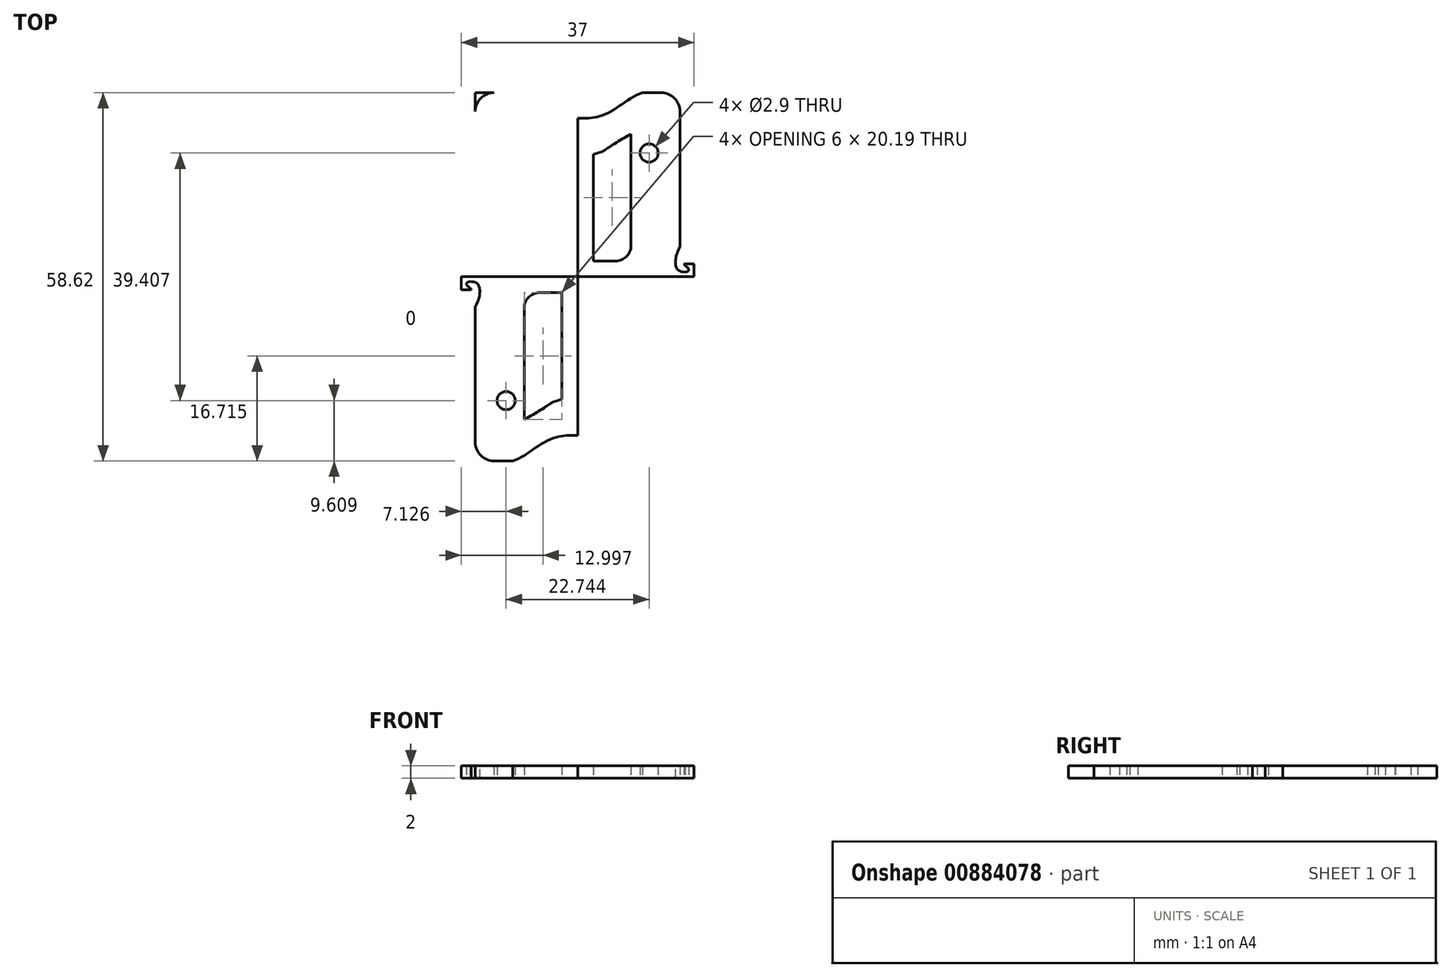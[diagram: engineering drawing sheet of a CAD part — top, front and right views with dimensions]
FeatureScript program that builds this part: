
annotation { "Feature Type Name" : "Feature", "Feature Type Description" : "" }
export const myFeature = defineFeature(function(context is Context, id is Id, definition is map)
    precondition{}
    {
        {
            var Q0;
            Q0=qCreatedBy(makeId("Top.planeOp"),FACE);
            var sketch = newSketch(context, id + "F0", { "sketchPlane" : qUnion([Q0])});
            skLineSegment(sketch, "E0.bottom", {"start": v(10.05, 48.23) * mm, "end": v(16.04, 48.23) * mm});
            skLineSegment(sketch, "E0.top", {"start": v(13.05, -10.39) * mm, "end": v(16.04, -10.39) * mm});
            skLineSegment(sketch, "E0.left", {"start": v(10.05, 48.23) * mm, "end": v(10.05, 23.75) * mm});
            skFitSpline(sketch, "E1", {"points": [v(42.63, 48.23) * mm, v(36.63, 48.23) * mm, v(30.94, 44.88) * mm, v(26.34, 44.13) * mm], "startDerivative": vector(-19.72, 0) * mm, "endDerivative": vector(-14.92, -0.07) * mm});
            skFitSpline(sketch, "E2.MirrorCS", {"points": [v(10.05, 48.23) * mm, v(16.04, 48.23) * mm, v(21.74, 44.88) * mm, v(26.34, 44.13) * mm], "startDerivative": vector(19.72, 0) * mm, "endDerivative": vector(14.92, -0.07) * mm});
            skFitSpline(sketch, "E3.MirrorCS", {"points": [v(42.63, -10.39) * mm, v(36.63, -10.39) * mm, v(30.94, -7.03) * mm, v(26.34, -6.29) * mm], "startDerivative": vector(-19.72, 0) * mm, "endDerivative": vector(-14.92, 0.07) * mm});
            skFitSpline(sketch, "E4.MirrorCS", {"points": [v(10.05, -10.39) * mm, v(16.04, -10.39) * mm, v(21.74, -7.03) * mm, v(26.34, -6.29) * mm], "startDerivative": vector(19.72, 0) * mm, "endDerivative": vector(14.92, 0.07) * mm});
            skLineSegment(sketch, "E5.trimOffspring", {"start": v(36.63, 48.23) * mm, "end": v(42.63, 48.23) * mm});
            skLineSegment(sketch, "E6.trimOffspring", {"start": v(36.63, -10.39) * mm, "end": v(42.63, -10.39) * mm});
            skArc(sketch, "E7.filletArc", {"start": v(10.05, -7.39) * mm, "mid": v(10.92, -9.5) * mm, "end": v(13.05, -10.39) * mm});
            skArc(sketch, "E8.MirrorCS", {"start": v(42.63, -7.39) * mm, "mid": v(41.75, -9.5) * mm, "end": v(39.63, -10.39) * mm});
            skArc(sketch, "E9.MirrorCS", {"start": v(42.63, 45.23) * mm, "mid": v(41.75, 47.35) * mm, "end": v(39.63, 48.23) * mm});
            skArc(sketch, "E10.MirrorCS", {"start": v(10.05, 45.23) * mm, "mid": v(10.92, 47.35) * mm, "end": v(13.05, 48.23) * mm});
            skCircle(sketch, "E11", {"center": v(14.97, 38.63) * mm, "radius": 1.45 * mm});
            skFitSpline(sketch, "E12", {"points": [v(10.05, 23.75) * mm, v(10.74, 20.73) * mm, v(9.24, 19.67) * mm], "startDerivative": vector(3.54, -6.71) * mm, "endDerivative": vector(-7.62, -0.35) * mm});
            skLineSegment(sketch, "E13", {"start": v(8.28, 20.96) * mm, "end": v(7.84, 20.96) * mm});
            skLineSegment(sketch, "E14", {"start": v(7.84, 20.96) * mm, "end": v(7.84, 18.92) * mm});
            skLineSegment(sketch, "E15.MirrorCS", {"start": v(7.84, 16.88) * mm, "end": v(7.84, 18.92) * mm});
            skLineSegment(sketch, "E16.MirrorCS", {"start": v(8.28, 16.88) * mm, "end": v(7.84, 16.88) * mm});
            skFitSpline(sketch, "E17.MirrorCS", {"points": [v(10.05, 14.1) * mm, v(10.74, 17.11) * mm, v(9.24, 18.18) * mm], "startDerivative": vector(3.54, 6.71) * mm, "endDerivative": vector(-7.62, 0.35) * mm});
            skLineSegment(sketch, "E18", {"start": v(8.28, 20.96) * mm, "end": v(9.38, 20.96) * mm});
            skFitSpline(sketch, "E19", {"points": [v(9.38, 20.96) * mm, v(8.76, 20.32) * mm, v(9.24, 19.67) * mm], "startDerivative": vector(0.5, -1.03) * mm, "endDerivative": vector(3.51, -0.24) * mm});
            skFitSpline(sketch, "E20.MirrorCS", {"points": [v(9.38, 16.88) * mm, v(8.76, 17.53) * mm, v(9.24, 18.18) * mm], "startDerivative": vector(0.5, 1.03) * mm, "endDerivative": vector(3.51, 0.24) * mm});
            skLineSegment(sketch, "E21.MirrorCS", {"start": v(8.28, 16.88) * mm, "end": v(9.38, 16.88) * mm});
            skPoint(sketch, "E22.orphan", {"position": v(8.28, 16.88) * mm});
            skLineSegment(sketch, "E23.trimOffspring", {"start": v(10.05, 14.1) * mm, "end": v(10.05, -7.39) * mm});
            skFitSpline(sketch, "E24.MirrorCS", {"points": [v(42.63, 23.75) * mm, v(41.94, 20.73) * mm, v(43.44, 19.67) * mm], "startDerivative": vector(-3.54, -6.71) * mm, "endDerivative": vector(7.62, -0.35) * mm});
            skFitSpline(sketch, "E25.MirrorCS", {"points": [v(42.63, 14.1) * mm, v(41.94, 17.11) * mm, v(43.44, 18.18) * mm], "startDerivative": vector(-3.54, 6.71) * mm, "endDerivative": vector(7.62, 0.35) * mm});
            skFitSpline(sketch, "E26.MirrorCS", {"points": [v(43.3, 16.88) * mm, v(43.91, 17.53) * mm, v(43.44, 18.18) * mm], "startDerivative": vector(-0.5, 1.03) * mm, "endDerivative": vector(-3.51, 0.24) * mm});
            skFitSpline(sketch, "E27.MirrorCS", {"points": [v(43.3, 20.96) * mm, v(43.91, 20.32) * mm, v(43.44, 19.67) * mm], "startDerivative": vector(-0.5, -1.03) * mm, "endDerivative": vector(-3.51, -0.24) * mm});
            skLineSegment(sketch, "E28.MirrorCS", {"start": v(44.4, 20.96) * mm, "end": v(43.3, 20.96) * mm});
            skLineSegment(sketch, "E29.MirrorCS", {"start": v(44.4, 20.96) * mm, "end": v(44.84, 20.96) * mm});
            skLineSegment(sketch, "E30.MirrorCS", {"start": v(44.4, 16.88) * mm, "end": v(43.3, 16.88) * mm});
            skLineSegment(sketch, "E31.MirrorCS", {"start": v(44.4, 16.88) * mm, "end": v(44.84, 16.88) * mm});
            skLineSegment(sketch, "E32.MirrorCS", {"start": v(44.84, 16.88) * mm, "end": v(44.84, 18.92) * mm});
            skLineSegment(sketch, "E33.MirrorCS", {"start": v(44.84, 20.96) * mm, "end": v(44.84, 18.92) * mm});
            skLineSegment(sketch, "E34", {"start": v(42.63, 45.23) * mm, "end": v(42.63, 23.75) * mm});
            skLineSegment(sketch, "E35", {"start": v(42.63, 14.1) * mm, "end": v(42.63, -7.39) * mm});
            skCircle(sketch, "E36.MirrorC", {"center": v(37.7, 38.63) * mm, "radius": 1.45 * mm});
            skLineSegment(sketch, "E37", {"start": v(26.34, 44.13) * mm, "end": v(26.34, -6.29) * mm});
            skLineSegment(sketch, "E38", {"start": v(7.84, 18.92) * mm, "end": v(44.84, 18.92) * mm});
            skCircle(sketch, "E39.MirrorC", {"center": v(14.97, -0.78) * mm, "radius": 1.45 * mm});
            skCircle(sketch, "E40.MirrorC", {"center": v(37.7, -0.78) * mm, "radius": 1.45 * mm});
            skLineSegment(sketch, "E41", {"start": v(23.84, 38.43) * mm, "end": v(23.84, 23.16) * mm});
            skLineSegment(sketch, "E42", {"start": v(22.23, 21.42) * mm, "end": v(20.34, 21.42) * mm});
            skLineSegment(sketch, "E43", {"start": v(17.84, 23.92) * mm, "end": v(17.84, 38.92) * mm});
            skPoint(sketch, "E44.visualSharp", {"position": v(23.84, 21.42) * mm});
            skPoint(sketch, "E45.visualSharp", {"position": v(17.84, 21.42) * mm});
            skArc(sketch, "E45.filletArc", {"start": v(17.84, 23.92) * mm, "mid": v(18.57, 22.15) * mm, "end": v(20.34, 21.42) * mm});
            skLineSegment(sketch, "E46", {"start": v(23.84, 23.16) * mm, "end": v(23.84, 21.42) * mm});
            skLineSegment(sketch, "E47", {"start": v(23.84, 21.42) * mm, "end": v(22.23, 21.42) * mm});
            skFitSpline(sketch, "E48.MirrorCS", {"points": [v(23.88, 38.42) * mm, v(21.77, 39.25) * mm, v(17.88, 41.61) * mm], "startDerivative": vector(-9.86, 2.36) * mm, "endDerivative": vector(-7.93, 3.79) * mm});
            skLineSegment(sketch, "E49", {"start": v(17.84, 38.92) * mm, "end": v(17.87, 41.62) * mm});
            skLineSegment(sketch, "E50", {"start": v(17.88, 41.61) * mm, "end": v(17.87, 41.62) * mm});
            skLineSegment(sketch, "E51.MirrorCS", {"start": v(34.8, 41.61) * mm, "end": v(34.8, 41.62) * mm});
            skLineSegment(sketch, "E52.MirrorCS", {"start": v(28.84, 21.42) * mm, "end": v(30.45, 21.42) * mm});
            skLineSegment(sketch, "E53.MirrorCS", {"start": v(28.84, 23.16) * mm, "end": v(28.84, 21.42) * mm});
            skPoint(sketch, "E54.MirrorP", {"position": v(28.84, 21.42) * mm});
            skLineSegment(sketch, "E55.MirrorCS", {"start": v(28.84, 38.43) * mm, "end": v(28.84, 23.16) * mm});
            skPoint(sketch, "E56.MirrorP", {"position": v(34.84, 21.42) * mm});
            skArc(sketch, "E57.MirrorCS", {"start": v(34.84, 23.92) * mm, "mid": v(34.1, 22.15) * mm, "end": v(32.34, 21.42) * mm});
            skLineSegment(sketch, "E58.MirrorCS", {"start": v(30.45, 21.42) * mm, "end": v(32.34, 21.42) * mm});
            skLineSegment(sketch, "E59.MirrorCS", {"start": v(34.84, 23.92) * mm, "end": v(34.84, 38.92) * mm});
            skLineSegment(sketch, "E60.MirrorCS", {"start": v(34.84, 38.92) * mm, "end": v(34.8, 41.62) * mm});
            skFitSpline(sketch, "E61.MirrorCS", {"points": [v(28.8, 38.42) * mm, v(30.9, 39.25) * mm, v(34.8, 41.61) * mm], "startDerivative": vector(9.86, 2.36) * mm, "endDerivative": vector(7.93, 3.79) * mm});
            skLineSegment(sketch, "E62.MirrorCS", {"start": v(34.8, -3.77) * mm, "end": v(34.8, -3.77) * mm});
            skLineSegment(sketch, "E63.MirrorCS", {"start": v(28.84, 16.42) * mm, "end": v(30.45, 16.42) * mm});
            skLineSegment(sketch, "E64.MirrorCS", {"start": v(28.84, 14.68) * mm, "end": v(28.84, 16.42) * mm});
            skPoint(sketch, "E65.MirrorP", {"position": v(28.84, 16.42) * mm});
            skLineSegment(sketch, "E66.MirrorCS", {"start": v(34.84, 13.92) * mm, "end": v(34.84, -1.08) * mm});
            skArc(sketch, "E67.MirrorCS", {"start": v(34.84, 13.92) * mm, "mid": v(34.1, 15.7) * mm, "end": v(32.34, 16.42) * mm});
            skLineSegment(sketch, "E68.MirrorCS", {"start": v(30.45, 16.42) * mm, "end": v(32.34, 16.42) * mm});
            skLineSegment(sketch, "E69.MirrorCS", {"start": v(28.84, -0.59) * mm, "end": v(28.84, 14.68) * mm});
            skFitSpline(sketch, "E70.MirrorCS", {"points": [v(28.8, -0.58) * mm, v(30.9, -1.4) * mm, v(34.8, -3.77) * mm], "startDerivative": vector(9.86, -2.36) * mm, "endDerivative": vector(7.93, -3.79) * mm});
            skLineSegment(sketch, "E71.MirrorCS", {"start": v(34.84, -1.08) * mm, "end": v(34.8, -3.77) * mm});
            skPoint(sketch, "E72.MirrorP", {"position": v(34.84, 16.42) * mm});
            skLineSegment(sketch, "E73.MirrorCS", {"start": v(17.88, -3.77) * mm, "end": v(17.87, -3.77) * mm});
            skLineSegment(sketch, "E74.MirrorCS", {"start": v(23.84, 16.42) * mm, "end": v(22.23, 16.42) * mm});
            skLineSegment(sketch, "E75.MirrorCS", {"start": v(23.84, 14.68) * mm, "end": v(23.84, 16.42) * mm});
            skLineSegment(sketch, "E76.MirrorCS", {"start": v(17.84, 13.92) * mm, "end": v(17.84, -1.08) * mm});
            skFitSpline(sketch, "E77.MirrorCS", {"points": [v(23.88, -0.58) * mm, v(21.77, -1.4) * mm, v(17.88, -3.77) * mm], "startDerivative": vector(-9.86, -2.36) * mm, "endDerivative": vector(-7.93, -3.79) * mm});
            skArc(sketch, "E78.MirrorCS", {"start": v(17.84, 13.92) * mm, "mid": v(18.57, 15.7) * mm, "end": v(20.34, 16.42) * mm});
            skLineSegment(sketch, "E79.MirrorCS", {"start": v(17.84, -1.08) * mm, "end": v(17.87, -3.77) * mm});
            skLineSegment(sketch, "E80.MirrorCS", {"start": v(23.84, -0.59) * mm, "end": v(23.84, 14.68) * mm});
            skLineSegment(sketch, "E81.MirrorCS", {"start": v(22.23, 16.42) * mm, "end": v(20.34, 16.42) * mm});
            skPoint(sketch, "E82.MirrorP", {"position": v(17.84, 16.42) * mm});
            skPoint(sketch, "E83.MirrorP", {"position": v(23.84, 16.42) * mm});
            skSolve(sketch);
        }
        {
            var Q0;
            {var subQ2=sQuery(id+"F0.wireOp",EDGE,"E10.MirrorCS");Q0=makeQuery(id+"F0.imprint","IMPRINT",FACE,{"disambiguationData":[TD([[makeQuery(id+"F0.imprint","IMPRINT",EDGE,{"derivedFrom":subQ2}),-1.0]])]});}
            var Q1;
            {var subQ1=sQuery(id+"F0.wireOp",EDGE,"E9.MirrorCS");Q1=makeQuery(id+"F0.imprint","IMPRINT",FACE,{"disambiguationData":[TD([[makeQuery(id+"F0.imprint","IMPRINT",EDGE,{"derivedFrom":subQ1}),1.0]])]});}
            var Q2;
            {var subQ1=sQuery(id+"F0.wireOp",EDGE,"E8.MirrorCS");Q2=makeQuery(id+"F0.imprint","IMPRINT",FACE,{"disambiguationData":[TD([[makeQuery(id+"F0.imprint","IMPRINT",EDGE,{"derivedFrom":subQ1}),-1.0]])]});}
            var Q3;
            {var subQ4=sQuery(id+"F0.wireOp",EDGE,"E0.top");Q3=makeQuery(id+"F0.imprint","IMPRINT",FACE,{"disambiguationData":[TD([[makeQuery(id+"F0.imprint","IMPRINT",EDGE,{"derivedFrom":subQ4}),1.0]])]});}
            extrude(context, id + "F1", {"entities" : qUnion([Q0, Q1, Q2, Q3]), "depth" : 2 * mm, "offsetDistance" : 25 * mm});
        }
    });
